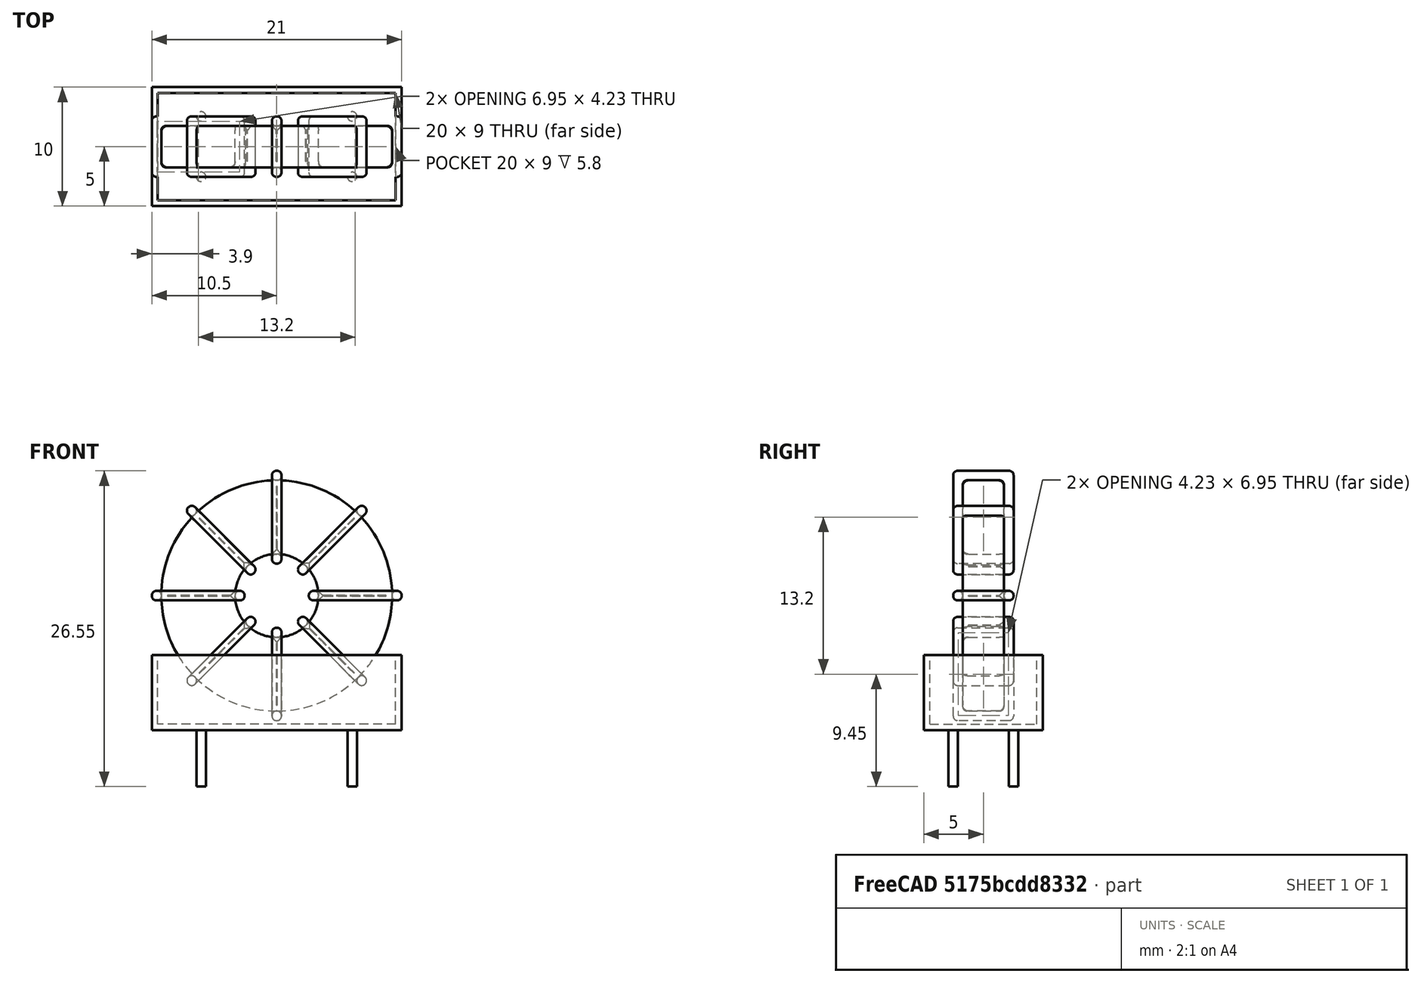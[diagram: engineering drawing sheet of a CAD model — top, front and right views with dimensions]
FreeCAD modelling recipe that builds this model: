
FCSTD DOCUMENT  (FreeCAD 0.16R6712 (Git))
Label: L_CommonMode_Toroid_Vertical_L21.0mm_W10.0mm_Px5.08mm_Py12.70mm_muRATA_5100
License: All rights reserved
LicenseURL: http://en.wikipedia.org/wiki/All_rights_reserved
objects: Sketcher::SketchObject×8, PartDesign::Pad×8, PartDesign::Fillet×5, Spreadsheet::Sheet×1, Part::MultiFuse×1
note: 30 computed .brp shape members not serialized (recipe doc carries the construction recipe); baked Part::Feature solids carry a one-line shape summary decoded from their .brp

FEATURE [Spreadsheet::Sheet] Spreadsheet  label="dimensions"
  cells = A1=Wx; B1(Wx)=21; C1(WW)=7; D1(iWx)=21; A2=Wy; B2(Wy)=5.08; D2(iWy)=10; A3=RM; B3(RMx)=5.08; C3(RMy)=12.7; A4=d_wire; B4(d_wire)=0.8; A5=H; B5(H)=31; A6=offsetx; B6(offsetx)=4.15
FEATURE [Sketcher::SketchObject] Sketch
  Placement = pos=(6.35,-2.54,0) rot=(1,0,0;1.5708rad)
  expr: Placement.Base.x = Spreadsheet.RMy / 2
  expr: Constraints[4] = Spreadsheet.WW / 2
  expr: Placement.Base.y = -Spreadsheet.RMx / 2
  expr: Constraints[0] = Spreadsheet.Wx / 2 - Spreadsheet.d_wire
  expr: Constraints[2] = Spreadsheet.Wx / 2 + Spreadsheet.d_wire + 0.5
  sketch-geometry (2):
    g0: Circle CenterX=0 CenterY=11.8 CenterZ=0 NormalX=0 NormalY=0 NormalZ=1 Radius=9.7
    g1: Circle CenterX=0 CenterY=11.8 CenterZ=0 NormalX=0 NormalY=0 NormalZ=1 Radius=3.5
  constraints (5):
    c: Radius(g0) = 9.7
    c: DistanceX(g-1,g0) = 0
    c: DistanceY(g-1,g0) = 11.8
    c: Coincident(g1,g0)
    c: Radius(g1) = 3.5
FEATURE [PartDesign::Pad] Pad
  Length = 3.48
  Length2 = 100
  Midplane = true
  Placement = pos=(6.35,-2.54,0) rot=(1,0,0;1.5708rad)
  Sketch = -> Sketch
  Type = 0
  expr: Length = Spreadsheet.Wy - 2 * Spreadsheet.d_wire
FEATURE [Sketcher::SketchObject] Sketch001
  Placement = pos=(0,0,0.75) rot=(0,0,1;0rad)
  expr: Constraints[4] = Spreadsheet.RMy
  expr: Constraints[2] = -Spreadsheet.RMx
  expr: Constraints[1] = Spreadsheet.d_wire / 2
  sketch-geometry (4):
    g0: Circle CenterX=0 CenterY=0 CenterZ=0 NormalX=0 NormalY=0 NormalZ=1 Radius=0.4
    g1: Circle CenterX=12.7 CenterY=-5.08 CenterZ=0 NormalX=0 NormalY=0 NormalZ=1 Radius=0.4
    g2: Circle CenterX=0 CenterY=-5.08 CenterZ=0 NormalX=0 NormalY=0 NormalZ=1 Radius=0.4
    g3: Circle CenterX=12.7 CenterY=0 CenterZ=0 NormalX=0 NormalY=0 NormalZ=1 Radius=0.4
  constraints (11):
    c: Equal(g0,g1)
    c: Radius(g0) = 0.4
    c: DistanceY(g-1,g1) = -5.08
    c: Coincident(g0,g-1)
    c: DistanceX(g-1,g1) = 12.7
    c: PointOnObject(g2,g-2)
    c: DistanceY(g-1,g3) = 0
    c: DistanceY(g2,g1) = 0
    c: DistanceX(g3,g1) = 0
    c: Equal(g3,g2)
    c: Equal(g2,g1)
FEATURE [PartDesign::Pad] Pad001
  Length = 5
  Length2 = 0
  Placement = pos=(0,0,0.75) rot=(0,0,1;0rad)
  Reversed = true
  Sketch = -> Sketch001
  Type = 0
FEATURE [PartDesign::Fillet] Fillet
  Base = -> Pad [Edge6,Edge3,Edge2]
  Placement = pos=(6.35,-2.54,0) rot=(1,0,0;1.5708rad)
  Radius = 0.5
FEATURE [Sketcher::SketchObject] Sketch003
  Placement = pos=(6.35,0,11.8) rot=(1,0,0;3.14159rad)
  expr: Placement.Base.x = Spreadsheet.RMy / 2
  expr: Constraints[18] = Spreadsheet.d_wire
  expr: Constraints[16] = Spreadsheet.d_wire
  expr: Constraints[19] = Spreadsheet.d_wire
  expr: Constraints[17] = Spreadsheet.d_wire
  expr: Placement.Base.y = -1 * (Spreadsheet.RMx - Spreadsheet.Wy) / 2
  expr: Constraints[21] = (Spreadsheet.Wx - Spreadsheet.WW) / 2 - Spreadsheet.d_wire
  expr: Constraints[22] = Spreadsheet.Wx / 2 - Spreadsheet.d_wire
  expr: Constraints[43] = Spreadsheet.d_wire
  expr: Constraints[48] = Spreadsheet.Wx - Spreadsheet.d_wire * 2
  expr: Constraints[49] = Spreadsheet.Wy
  expr: Placement.Base.z = Spreadsheet.Wx / 2 + Spreadsheet.d_wire + 0.5
  sketch-geometry (16):
    g0: LineSegment StartX=-2.7 StartY=0 StartZ=0 EndX=-10.5 EndY=0 EndZ=0
    g1: LineSegment StartX=-10.5 StartY=0 StartZ=0 EndX=-10.5 EndY=5.08 EndZ=0
    g2: LineSegment StartX=-10.5 StartY=5.08 StartZ=0 EndX=-2.7 EndY=5.08 EndZ=0
    g3: LineSegment StartX=-2.7 StartY=5.08 StartZ=0 EndX=-2.7 EndY=0 EndZ=0
    g4: LineSegment StartX=-9.7 StartY=4.28 StartZ=0 EndX=-3.5 EndY=4.28 EndZ=0
    g5: LineSegment StartX=-3.5 StartY=4.28 StartZ=0 EndX=-3.5 EndY=0.8 EndZ=0
    g6: LineSegment StartX=-3.5 StartY=0.8 StartZ=0 EndX=-9.7 EndY=0.8 EndZ=0
    g7: LineSegment StartX=-9.7 StartY=0.8 StartZ=0 EndX=-9.7 EndY=4.28 EndZ=0
    g8: LineSegment StartX=2.7 StartY=5.08 StartZ=0 EndX=10.5 EndY=5.08 EndZ=0
    g9: LineSegment StartX=10.5 StartY=5.08 StartZ=0 EndX=10.5 EndY=0 EndZ=0
    g10: LineSegment StartX=10.5 StartY=0 StartZ=0 EndX=2.7 EndY=0 EndZ=0
    g11: LineSegment StartX=2.7 StartY=0 StartZ=0 EndX=2.7 EndY=5.08 EndZ=0
    g12: LineSegment StartX=3.5 StartY=4.28 StartZ=0 EndX=9.7 EndY=4.28 EndZ=0
    g13: LineSegment StartX=9.7 StartY=4.28 StartZ=0 EndX=9.7 EndY=0.8 EndZ=0
    g14: LineSegment StartX=9.7 StartY=0.8 StartZ=0 EndX=3.5 EndY=0.8 EndZ=0
    g15: LineSegment StartX=3.5 StartY=0.8 StartZ=0 EndX=3.5 EndY=4.28 EndZ=0
  constraints (50):
    c: Horizontal(g0)
    c: Coincident(g1,g0)
    c: Vertical(g1)
    c: Coincident(g2,g1)
    c: Horizontal(g2)
    c: Coincident(g3,g2)
    c: Coincident(g3,g0)
    c: Vertical(g3)
    c: Coincident(g4,g5)
    c: Coincident(g5,g6)
    c: Coincident(g6,g7)
    c: Coincident(g7,g4)
    c: Horizontal(g4)
    c: Horizontal(g6)
    c: Vertical(g5)
    c: Vertical(g7)
    c: DistanceX(g1,g4) = 0.8
    c: DistanceY(g4,g1) = 0.8
    c: DistanceX(g5,g0) = 0.8
    c: DistanceY(g0,g5) = 0.8
    c: DistanceY(g-1,g0) = 0
    c: DistanceX(g6,g6) = 6.2
    c: DistanceX(g6,g-1) = 9.7
    c: Coincident(g8,g9)
    c: Coincident(g9,g10)
    c: Coincident(g10,g11)
    c: Coincident(g11,g8)
    c: Horizontal(g8)
    c: Horizontal(g10)
    c: Vertical(g9)
    c: Vertical(g11)
    c: Coincident(g12,g13)
    c: Coincident(g13,g14)
    c: Coincident(g14,g15)
    c: Coincident(g15,g12)
    c: Horizontal(g12)
    c: Horizontal(g14)
    c: Vertical(g13)
    c: Vertical(g15)
    c: DistanceY(g8,g2) = 0
    c: DistanceY(g10,g0) = 0
    c: DistanceY(g14,g5) = 0
    c: DistanceY(g12,g4) = 0
    c: DistanceX(g8,g12) = 0.8
    c: Equal(g8,g2)
    c: Equal(g12,g4)
    c: Equal(g9,g1)
    c: Equal(g13,g7)
    c: DistanceX(g4,g12) = 19.4
    c: DistanceY(g0,g1) = 5.08
FEATURE [PartDesign::Pad] Pad002
  Length = 0.8
  Length2 = 100
  Midplane = true
  Placement = pos=(6.35,0,11.8) rot=(1,0,0;3.14159rad)
  Sketch = -> Sketch003
  Type = 0
  expr: Length = Spreadsheet.d_wire
FEATURE [PartDesign::Fillet] Fillet001
  Base = -> Pad002 [Edge38,Edge41,Edge42,Edge43,Edge29,Edge32,Edge33,Edge34,Edge25,Edge35,Edge36,Edge13,Edge14,Edge15,Edge16,Edge17,Edge18,Edge19,Edge1,Edge2,Edge3,Edge4,Edge5,Edge6,Edge7,Edge37,Edge39,Edge40,Edge20,Edge23,Edge24,Edge21,Edge22,Edge8,Edge9,Edge10,Edge11,Edge12,Edge26,Edge27,+8 more]
  Placement = pos=(6.35,0,11.8) rot=(1,0,0;3.14159rad)
  Radius = 0.376
  expr: Radius = Spreadsheet.d_wire * 0.47
FEATURE [Sketcher::SketchObject] Sketch004
  Placement = pos=(6.35,0,11.8) rot=(0.92388,0,0.382683;3.14159rad)
  expr: Placement.Base.x = Spreadsheet.RMy / 2
  expr: Constraints[18] = Spreadsheet.d_wire
  expr: Constraints[16] = Spreadsheet.d_wire
  expr: Constraints[19] = Spreadsheet.d_wire
  expr: Constraints[17] = Spreadsheet.d_wire
  expr: Placement.Base.y = -1 * (Spreadsheet.RMx - Spreadsheet.Wy) / 2
  expr: Constraints[21] = (Spreadsheet.Wx - Spreadsheet.WW) / 2 - Spreadsheet.d_wire
  expr: Constraints[22] = Spreadsheet.Wx / 2 - Spreadsheet.d_wire
  expr: Constraints[43] = Spreadsheet.d_wire
  expr: Constraints[48] = Spreadsheet.Wx - 2 * Spreadsheet.d_wire
  expr: Constraints[49] = Spreadsheet.Wy
  expr: Placement.Base.z = Spreadsheet.Wx / 2 + Spreadsheet.d_wire + 0.5
  sketch-geometry (16):
    g0: LineSegment StartX=-2.7 StartY=0 StartZ=0 EndX=-10.5 EndY=0 EndZ=0
    g1: LineSegment StartX=-10.5 StartY=0 StartZ=0 EndX=-10.5 EndY=5.08 EndZ=0
    g2: LineSegment StartX=-10.5 StartY=5.08 StartZ=0 EndX=-2.7 EndY=5.08 EndZ=0
    g3: LineSegment StartX=-2.7 StartY=5.08 StartZ=0 EndX=-2.7 EndY=0 EndZ=0
    g4: LineSegment StartX=-9.7 StartY=4.28 StartZ=0 EndX=-3.5 EndY=4.28 EndZ=0
    g5: LineSegment StartX=-3.5 StartY=4.28 StartZ=0 EndX=-3.5 EndY=0.8 EndZ=0
    g6: LineSegment StartX=-3.5 StartY=0.8 StartZ=0 EndX=-9.7 EndY=0.8 EndZ=0
    g7: LineSegment StartX=-9.7 StartY=0.8 StartZ=0 EndX=-9.7 EndY=4.28 EndZ=0
    g8: LineSegment StartX=2.7 StartY=5.08 StartZ=0 EndX=10.5 EndY=5.08 EndZ=0
    g9: LineSegment StartX=10.5 StartY=5.08 StartZ=0 EndX=10.5 EndY=0 EndZ=0
    g10: LineSegment StartX=10.5 StartY=0 StartZ=0 EndX=2.7 EndY=0 EndZ=0
    g11: LineSegment StartX=2.7 StartY=0 StartZ=0 EndX=2.7 EndY=5.08 EndZ=0
    g12: LineSegment StartX=3.5 StartY=4.28 StartZ=0 EndX=9.7 EndY=4.28 EndZ=0
    g13: LineSegment StartX=9.7 StartY=4.28 StartZ=0 EndX=9.7 EndY=0.8 EndZ=0
    g14: LineSegment StartX=9.7 StartY=0.8 StartZ=0 EndX=3.5 EndY=0.8 EndZ=0
    g15: LineSegment StartX=3.5 StartY=0.8 StartZ=0 EndX=3.5 EndY=4.28 EndZ=0
  constraints (50):
    c: Horizontal(g0)
    c: Coincident(g1,g0)
    c: Vertical(g1)
    c: Coincident(g2,g1)
    c: Horizontal(g2)
    c: Coincident(g3,g2)
    c: Coincident(g3,g0)
    c: Vertical(g3)
    c: Coincident(g4,g5)
    c: Coincident(g5,g6)
    c: Coincident(g6,g7)
    c: Coincident(g7,g4)
    c: Horizontal(g4)
    c: Horizontal(g6)
    c: Vertical(g5)
    c: Vertical(g7)
    c: DistanceX(g1,g4) = 0.8
    c: DistanceY(g4,g1) = 0.8
    c: DistanceX(g5,g0) = 0.8
    c: DistanceY(g0,g5) = 0.8
    c: DistanceY(g-1,g0) = 0
    c: DistanceX(g6,g6) = 6.2
    c: DistanceX(g6,g-1) = 9.7
    c: Coincident(g8,g9)
    c: Coincident(g9,g10)
    c: Coincident(g10,g11)
    c: Coincident(g11,g8)
    c: Horizontal(g8)
    c: Horizontal(g10)
    c: Vertical(g9)
    c: Vertical(g11)
    c: Coincident(g12,g13)
    c: Coincident(g13,g14)
    c: Coincident(g14,g15)
    c: Coincident(g15,g12)
    c: Horizontal(g12)
    c: Horizontal(g14)
    c: Vertical(g13)
    c: Vertical(g15)
    c: DistanceY(g8,g2) = 0
    c: DistanceY(g10,g0) = 0
    c: DistanceY(g14,g5) = 0
    c: DistanceY(g12,g4) = 0
    c: DistanceX(g8,g12) = 0.8
    c: Equal(g8,g2)
    c: Equal(g12,g4)
    c: Equal(g9,g1)
    c: Equal(g13,g7)
    c: DistanceX(g4,g12) = 19.4
    c: DistanceY(g0,g1) = 5.08
FEATURE [PartDesign::Pad] Pad003
  Length = 0.8
  Length2 = 100
  Midplane = true
  Placement = pos=(6.35,0,11.8) rot=(0.92388,0,0.382683;3.14159rad)
  Sketch = -> Sketch004
  Type = 0
  expr: Length = Spreadsheet.d_wire
FEATURE [PartDesign::Fillet] Fillet002
  Base = -> Pad003 [Edge38,Edge41,Edge42,Edge43,Edge29,Edge32,Edge33,Edge34,Edge25,Edge35,Edge36,Edge13,Edge14,Edge15,Edge16,Edge17,Edge18,Edge19,Edge1,Edge2,Edge3,Edge4,Edge5,Edge6,Edge7,Edge37,Edge39,Edge40,Edge20,Edge23,Edge24,Edge21,Edge22,Edge8,Edge9,Edge10,Edge11,Edge12,Edge26,Edge27,+8 more]
  Placement = pos=(6.35,0,11.8) rot=(0.92388,0,0.382683;3.14159rad)
  Radius = 0.376
  expr: Radius = Spreadsheet.d_wire * 0.47
FEATURE [Sketcher::SketchObject] Sketch005
  Placement = pos=(6.35,0,11.8) rot=(0.92388,0,-0.382683;3.14159rad)
  expr: Placement.Base.x = Spreadsheet.RMy / 2
  expr: Constraints[18] = Spreadsheet.d_wire
  expr: Constraints[16] = Spreadsheet.d_wire
  expr: Constraints[19] = Spreadsheet.d_wire
  expr: Constraints[17] = Spreadsheet.d_wire
  expr: Placement.Base.y = -1 * (Spreadsheet.RMx - Spreadsheet.Wy) / 2
  expr: Constraints[21] = (Spreadsheet.Wx - Spreadsheet.WW) / 2 - Spreadsheet.d_wire
  expr: Constraints[22] = Spreadsheet.Wx / 2 - Spreadsheet.d_wire
  expr: Constraints[43] = Spreadsheet.d_wire
  expr: Constraints[48] = Spreadsheet.Wx - 2 * Spreadsheet.d_wire
  expr: Constraints[49] = Spreadsheet.Wy
  expr: Placement.Base.z = Spreadsheet.Wx / 2 + Spreadsheet.d_wire + 0.5
  sketch-geometry (16):
    g0: LineSegment StartX=-2.7 StartY=0 StartZ=0 EndX=-10.5 EndY=0 EndZ=0
    g1: LineSegment StartX=-10.5 StartY=0 StartZ=0 EndX=-10.5 EndY=5.08 EndZ=0
    g2: LineSegment StartX=-10.5 StartY=5.08 StartZ=0 EndX=-2.7 EndY=5.08 EndZ=0
    g3: LineSegment StartX=-2.7 StartY=5.08 StartZ=0 EndX=-2.7 EndY=0 EndZ=0
    g4: LineSegment StartX=-9.7 StartY=4.28 StartZ=0 EndX=-3.5 EndY=4.28 EndZ=0
    g5: LineSegment StartX=-3.5 StartY=4.28 StartZ=0 EndX=-3.5 EndY=0.8 EndZ=0
    g6: LineSegment StartX=-3.5 StartY=0.8 StartZ=0 EndX=-9.7 EndY=0.8 EndZ=0
    g7: LineSegment StartX=-9.7 StartY=0.8 StartZ=0 EndX=-9.7 EndY=4.28 EndZ=0
    g8: LineSegment StartX=2.7 StartY=5.08 StartZ=0 EndX=10.5 EndY=5.08 EndZ=0
    g9: LineSegment StartX=10.5 StartY=5.08 StartZ=0 EndX=10.5 EndY=0 EndZ=0
    g10: LineSegment StartX=10.5 StartY=0 StartZ=0 EndX=2.7 EndY=0 EndZ=0
    g11: LineSegment StartX=2.7 StartY=0 StartZ=0 EndX=2.7 EndY=5.08 EndZ=0
    g12: LineSegment StartX=3.5 StartY=4.28 StartZ=0 EndX=9.7 EndY=4.28 EndZ=0
    g13: LineSegment StartX=9.7 StartY=4.28 StartZ=0 EndX=9.7 EndY=0.8 EndZ=0
    g14: LineSegment StartX=9.7 StartY=0.8 StartZ=0 EndX=3.5 EndY=0.8 EndZ=0
    g15: LineSegment StartX=3.5 StartY=0.8 StartZ=0 EndX=3.5 EndY=4.28 EndZ=0
  constraints (50):
    c: Horizontal(g0)
    c: Coincident(g1,g0)
    c: Vertical(g1)
    c: Coincident(g2,g1)
    c: Horizontal(g2)
    c: Coincident(g3,g2)
    c: Coincident(g3,g0)
    c: Vertical(g3)
    c: Coincident(g4,g5)
    c: Coincident(g5,g6)
    c: Coincident(g6,g7)
    c: Coincident(g7,g4)
    c: Horizontal(g4)
    c: Horizontal(g6)
    c: Vertical(g5)
    c: Vertical(g7)
    c: DistanceX(g1,g4) = 0.8
    c: DistanceY(g4,g1) = 0.8
    c: DistanceX(g5,g0) = 0.8
    c: DistanceY(g0,g5) = 0.8
    c: DistanceY(g-1,g0) = 0
    c: DistanceX(g6,g6) = 6.2
    c: DistanceX(g6,g-1) = 9.7
    c: Coincident(g8,g9)
    c: Coincident(g9,g10)
    c: Coincident(g10,g11)
    c: Coincident(g11,g8)
    c: Horizontal(g8)
    c: Horizontal(g10)
    c: Vertical(g9)
    c: Vertical(g11)
    c: Coincident(g12,g13)
    c: Coincident(g13,g14)
    c: Coincident(g14,g15)
    c: Coincident(g15,g12)
    c: Horizontal(g12)
    c: Horizontal(g14)
    c: Vertical(g13)
    c: Vertical(g15)
    c: DistanceY(g8,g2) = 0
    c: DistanceY(g10,g0) = 0
    c: DistanceY(g14,g5) = 0
    c: DistanceY(g12,g4) = 0
    c: DistanceX(g8,g12) = 0.8
    c: Equal(g8,g2)
    c: Equal(g12,g4)
    c: Equal(g9,g1)
    c: Equal(g13,g7)
    c: DistanceX(g4,g12) = 19.4
    c: DistanceY(g0,g1) = 5.08
FEATURE [PartDesign::Pad] Pad004
  Length = 0.8
  Length2 = 100
  Midplane = true
  Placement = pos=(6.35,0,11.8) rot=(0.92388,0,-0.382683;3.14159rad)
  Sketch = -> Sketch005
  Type = 0
  expr: Length = Spreadsheet.d_wire
FEATURE [PartDesign::Fillet] Fillet003
  Base = -> Pad004 [Edge38,Edge41,Edge42,Edge43,Edge29,Edge32,Edge33,Edge34,Edge25,Edge35,Edge36,Edge13,Edge14,Edge15,Edge16,Edge17,Edge18,Edge19,Edge1,Edge2,Edge3,Edge4,Edge5,Edge6,Edge7,Edge37,Edge39,Edge40,Edge20,Edge23,Edge24,Edge21,Edge22,Edge8,Edge9,Edge10,Edge11,Edge12,Edge26,Edge27,+8 more]
  Placement = pos=(6.35,0,11.8) rot=(0.92388,0,-0.382683;3.14159rad)
  Radius = 0.376
  expr: Radius = Spreadsheet.d_wire * 0.47
FEATURE [Sketcher::SketchObject] Sketch006
  Placement = pos=(6.35,0,11.8) rot=(0.707107,0,0.707107;3.14159rad)
  expr: Placement.Base.x = Spreadsheet.RMy / 2
  expr: Constraints[18] = Spreadsheet.d_wire
  expr: Constraints[16] = Spreadsheet.d_wire
  expr: Constraints[19] = Spreadsheet.d_wire
  expr: Constraints[17] = Spreadsheet.d_wire
  expr: Placement.Base.y = -1 * (Spreadsheet.RMx - Spreadsheet.Wy) / 2
  expr: Constraints[21] = (Spreadsheet.Wx - Spreadsheet.WW) / 2 - Spreadsheet.d_wire
  expr: Constraints[22] = Spreadsheet.Wx / 2 - Spreadsheet.d_wire
  expr: Constraints[43] = Spreadsheet.d_wire
  expr: Constraints[48] = Spreadsheet.Wx - Spreadsheet.d_wire * 2
  expr: Constraints[49] = Spreadsheet.Wy
  expr: Placement.Base.z = Spreadsheet.Wx / 2 + Spreadsheet.d_wire + 0.5
  sketch-geometry (16):
    g0: LineSegment StartX=-2.7 StartY=0 StartZ=0 EndX=-10.5 EndY=0 EndZ=0
    g1: LineSegment StartX=-10.5 StartY=0 StartZ=0 EndX=-10.5 EndY=5.08 EndZ=0
    g2: LineSegment StartX=-10.5 StartY=5.08 StartZ=0 EndX=-2.7 EndY=5.08 EndZ=0
    g3: LineSegment StartX=-2.7 StartY=5.08 StartZ=0 EndX=-2.7 EndY=0 EndZ=0
    g4: LineSegment StartX=-9.7 StartY=4.28 StartZ=0 EndX=-3.5 EndY=4.28 EndZ=0
    g5: LineSegment StartX=-3.5 StartY=4.28 StartZ=0 EndX=-3.5 EndY=0.8 EndZ=0
    g6: LineSegment StartX=-3.5 StartY=0.8 StartZ=0 EndX=-9.7 EndY=0.8 EndZ=0
    g7: LineSegment StartX=-9.7 StartY=0.8 StartZ=0 EndX=-9.7 EndY=4.28 EndZ=0
    g8: LineSegment StartX=2.7 StartY=5.08 StartZ=0 EndX=10.5 EndY=5.08 EndZ=0
    g9: LineSegment StartX=10.5 StartY=5.08 StartZ=0 EndX=10.5 EndY=0 EndZ=0
    g10: LineSegment StartX=10.5 StartY=0 StartZ=0 EndX=2.7 EndY=0 EndZ=0
    g11: LineSegment StartX=2.7 StartY=0 StartZ=0 EndX=2.7 EndY=5.08 EndZ=0
    g12: LineSegment StartX=3.5 StartY=4.28 StartZ=0 EndX=9.7 EndY=4.28 EndZ=0
    g13: LineSegment StartX=9.7 StartY=4.28 StartZ=0 EndX=9.7 EndY=0.8 EndZ=0
    g14: LineSegment StartX=9.7 StartY=0.8 StartZ=0 EndX=3.5 EndY=0.8 EndZ=0
    g15: LineSegment StartX=3.5 StartY=0.8 StartZ=0 EndX=3.5 EndY=4.28 EndZ=0
  constraints (50):
    c: Horizontal(g0)
    c: Coincident(g1,g0)
    c: Vertical(g1)
    c: Coincident(g2,g1)
    c: Horizontal(g2)
    c: Coincident(g3,g2)
    c: Coincident(g3,g0)
    c: Vertical(g3)
    c: Coincident(g4,g5)
    c: Coincident(g5,g6)
    c: Coincident(g6,g7)
    c: Coincident(g7,g4)
    c: Horizontal(g4)
    c: Horizontal(g6)
    c: Vertical(g5)
    c: Vertical(g7)
    c: DistanceX(g1,g4) = 0.8
    c: DistanceY(g4,g1) = 0.8
    c: DistanceX(g5,g0) = 0.8
    c: DistanceY(g0,g5) = 0.8
    c: DistanceY(g-1,g0) = 0
    c: DistanceX(g6,g6) = 6.2
    c: DistanceX(g6,g-1) = 9.7
    c: Coincident(g8,g9)
    c: Coincident(g9,g10)
    c: Coincident(g10,g11)
    c: Coincident(g11,g8)
    c: Horizontal(g8)
    c: Horizontal(g10)
    c: Vertical(g9)
    c: Vertical(g11)
    c: Coincident(g12,g13)
    c: Coincident(g13,g14)
    c: Coincident(g14,g15)
    c: Coincident(g15,g12)
    c: Horizontal(g12)
    c: Horizontal(g14)
    c: Vertical(g13)
    c: Vertical(g15)
    c: DistanceY(g8,g2) = 0
    c: DistanceY(g10,g0) = 0
    c: DistanceY(g14,g5) = 0
    c: DistanceY(g12,g4) = 0
    c: DistanceX(g8,g12) = 0.8
    c: Equal(g8,g2)
    c: Equal(g12,g4)
    c: Equal(g9,g1)
    c: Equal(g13,g7)
    c: DistanceX(g4,g12) = 19.4
    c: DistanceY(g0,g1) = 5.08
FEATURE [PartDesign::Pad] Pad005
  Length = 0.8
  Length2 = 100
  Midplane = true
  Placement = pos=(6.35,0,11.8) rot=(0.707107,0,0.707107;3.14159rad)
  Sketch = -> Sketch006
  Type = 0
  expr: Length = Spreadsheet.d_wire
FEATURE [PartDesign::Fillet] Fillet004
  Base = -> Pad005 [Edge38,Edge41,Edge42,Edge43,Edge29,Edge32,Edge33,Edge34,Edge25,Edge35,Edge36,Edge13,Edge14,Edge15,Edge16,Edge17,Edge18,Edge19,Edge1,Edge2,Edge3,Edge4,Edge5,Edge6,Edge7,Edge37,Edge39,Edge40,Edge20,Edge23,Edge24,Edge21,Edge22,Edge8,Edge9,Edge10,Edge11,Edge12,Edge26,Edge27,+8 more]
  Placement = pos=(6.35,0,11.8) rot=(0.707107,0,0.707107;3.14159rad)
  Radius = 0.376
  expr: Radius = Spreadsheet.d_wire * 0.47
FEATURE [Sketcher::SketchObject] Sketch007
  Placement = pos=(6.35,0,0.5) rot=(0,0,1;0rad)
  expr: Placement.Base.x = Spreadsheet.RMy / 2
  expr: Placement.Base.z = 0.5
  expr: Constraints[11] = Spreadsheet.iWx / 2
  expr: Constraints[10] = (Spreadsheet.iWy - Spreadsheet.RMx) / 2
  expr: Constraints[9] = Spreadsheet.iWy
  expr: Constraints[8] = Spreadsheet.iWx
  sketch-geometry (4):
    g0: LineSegment StartX=-10.5 StartY=2.46 StartZ=0 EndX=10.5 EndY=2.46 EndZ=0
    g1: LineSegment StartX=10.5 StartY=2.46 StartZ=0 EndX=10.5 EndY=-7.54 EndZ=0
    g2: LineSegment StartX=10.5 StartY=-7.54 StartZ=0 EndX=-10.5 EndY=-7.54 EndZ=0
    g3: LineSegment StartX=-10.5 StartY=-7.54 StartZ=0 EndX=-10.5 EndY=2.46 EndZ=0
  constraints (12):
    c: Coincident(g0,g1)
    c: Coincident(g1,g2)
    c: Coincident(g2,g3)
    c: Coincident(g3,g0)
    c: Horizontal(g0)
    c: Horizontal(g2)
    c: Vertical(g1)
    c: Vertical(g3)
    c: DistanceX(g0,g0) = 21
    c: DistanceY(g3,g3) = 10
    c: DistanceY(g-1,g0) = 2.46
    c: DistanceX(g0,g-1) = 10.5
FEATURE [PartDesign::Pad] Pad006
  Length = 0.5
  Length2 = 100
  Placement = pos=(6.35,0,0.5) rot=(0,0,1;0rad)
  Sketch = -> Sketch007
  Type = 0
FEATURE [Sketcher::SketchObject] Sketch008
  Placement = pos=(6.35,0,0.5) rot=(0,0,1;0rad)
  expr: Placement.Base.x = Spreadsheet.RMy / 2
  expr: Constraints[8] = Spreadsheet.iWx
  expr: Constraints[9] = Spreadsheet.iWy
  expr: Constraints[10] = (Spreadsheet.iWy - Spreadsheet.RMx) / 2
  expr: Placement.Base.z = 0.5
  expr: Constraints[21] = 0.5
  expr: Constraints[11] = Spreadsheet.iWx / 2
  sketch-geometry (8):
    g0: LineSegment StartX=-10.5 StartY=2.46 StartZ=0 EndX=10.5 EndY=2.46 EndZ=0
    g1: LineSegment StartX=10.5 StartY=2.46 StartZ=0 EndX=10.5 EndY=-7.54 EndZ=0
    g2: LineSegment StartX=10.5 StartY=-7.54 StartZ=0 EndX=-10.5 EndY=-7.54 EndZ=0
    g3: LineSegment StartX=-10.5 StartY=-7.54 StartZ=0 EndX=-10.5 EndY=2.46 EndZ=0
    g4: LineSegment StartX=-10 StartY=1.96 StartZ=0 EndX=10 EndY=1.96 EndZ=0
    g5: LineSegment StartX=10 StartY=1.96 StartZ=0 EndX=10 EndY=-7.04 EndZ=0
    g6: LineSegment StartX=10 StartY=-7.04 StartZ=0 EndX=-10 EndY=-7.04 EndZ=0
    g7: LineSegment StartX=-10 StartY=-7.04 StartZ=0 EndX=-10 EndY=1.96 EndZ=0
  constraints (24):
    c: Coincident(g0,g1)
    c: Coincident(g1,g2)
    c: Coincident(g2,g3)
    c: Coincident(g3,g0)
    c: Horizontal(g0)
    c: Horizontal(g2)
    c: Vertical(g1)
    c: Vertical(g3)
    c: DistanceX(g0,g0) = 21
    c: DistanceY(g3,g3) = 10
    c: DistanceY(g-1,g0) = 2.46
    c: DistanceX(g0,g-1) = 10.5
    c: Coincident(g4,g5)
    c: Coincident(g5,g6)
    c: Coincident(g6,g7)
    c: Coincident(g7,g4)
    c: Horizontal(g4)
    c: Horizontal(g6)
    c: Vertical(g5)
    c: Vertical(g7)
    c: DistanceX(g5,g1) = 0.5
    c: DistanceY(g1,g5) = 0.5
    c: DistanceX(g0,g4) = 0.5
    c: DistanceY(g4,g0) = 0.5
FEATURE [PartDesign::Pad] Pad007
  Length = 6.3
  Length2 = 100
  Placement = pos=(6.35,0,0.5) rot=(0,0,1;0rad)
  Sketch = -> Sketch008
  Type = 0
  expr: Length = Spreadsheet.Wx * 0.3
FEATURE [Part::MultiFuse] Pad001_mp_cp  label="L_CommonMode_Toroid_Vertical_L21.0mm_W10.0mm_Px5.08mm_Py12.70mm_muRATA_5100"
  Shapes = -> [Pad001,Fillet,Fillet001,Fillet002,Fillet003,Fillet004,Pad006,Pad007]
